# Revit family: Water_Heater_Manifolds-Navien-NCB-Primary-03
name_source: partatom
category: Pipe Fittings
revit_build: Autodesk Revit 2016 (Build: 20150220_1215(x64)
units: mm (PartAtom-declared; Revit-internal decimal feet)

## family parameters
Always vertical = Yes
Cut with Voids When Loaded = No
OmniClass Number = 23.60.30.11.14
OmniClass Title = Pipework Fittings
Part Type = Multi Port
Round Connector Dimension = Use Radius
Shared = No
Work Plane-Based = No

## types (1)
- NCB Manifold
    Assembly Code = D3010500
    Boiler Heating Return Connection = 0' - 1"
    Boiler Heating Supply Connection = 0' - 1"
    Description = NCB Primary Manifolds
    Finish = Metal - Navien - Copper
    Heating Return = 0' - 1 1/4"
    Heating Supply = 0' - 1 1/4"
    K Coefficient Table = Tee
    Keynote = 22 33 00.A1
    Loss Method = Not Defined
    Manufacturer = Navien, Inc.
    Manufacturer Fax Number = (949) 420-0430
    Material = Produced with durable L-Copper piping
    Model = GFFM-MCOZUS-001
    Product Documentation Link = https://www.navieninc.com
    Product Name = Manifold
    Product Page URL = https://www.navieninc.com
    URL = https://www.navieninc.com
    Version = 2016 - v1.0.a
    Weight = 9.00 lbf

## geometry (parser evidence)
native form markers: Sweep x1
no freeform markers — native parametric forms only
